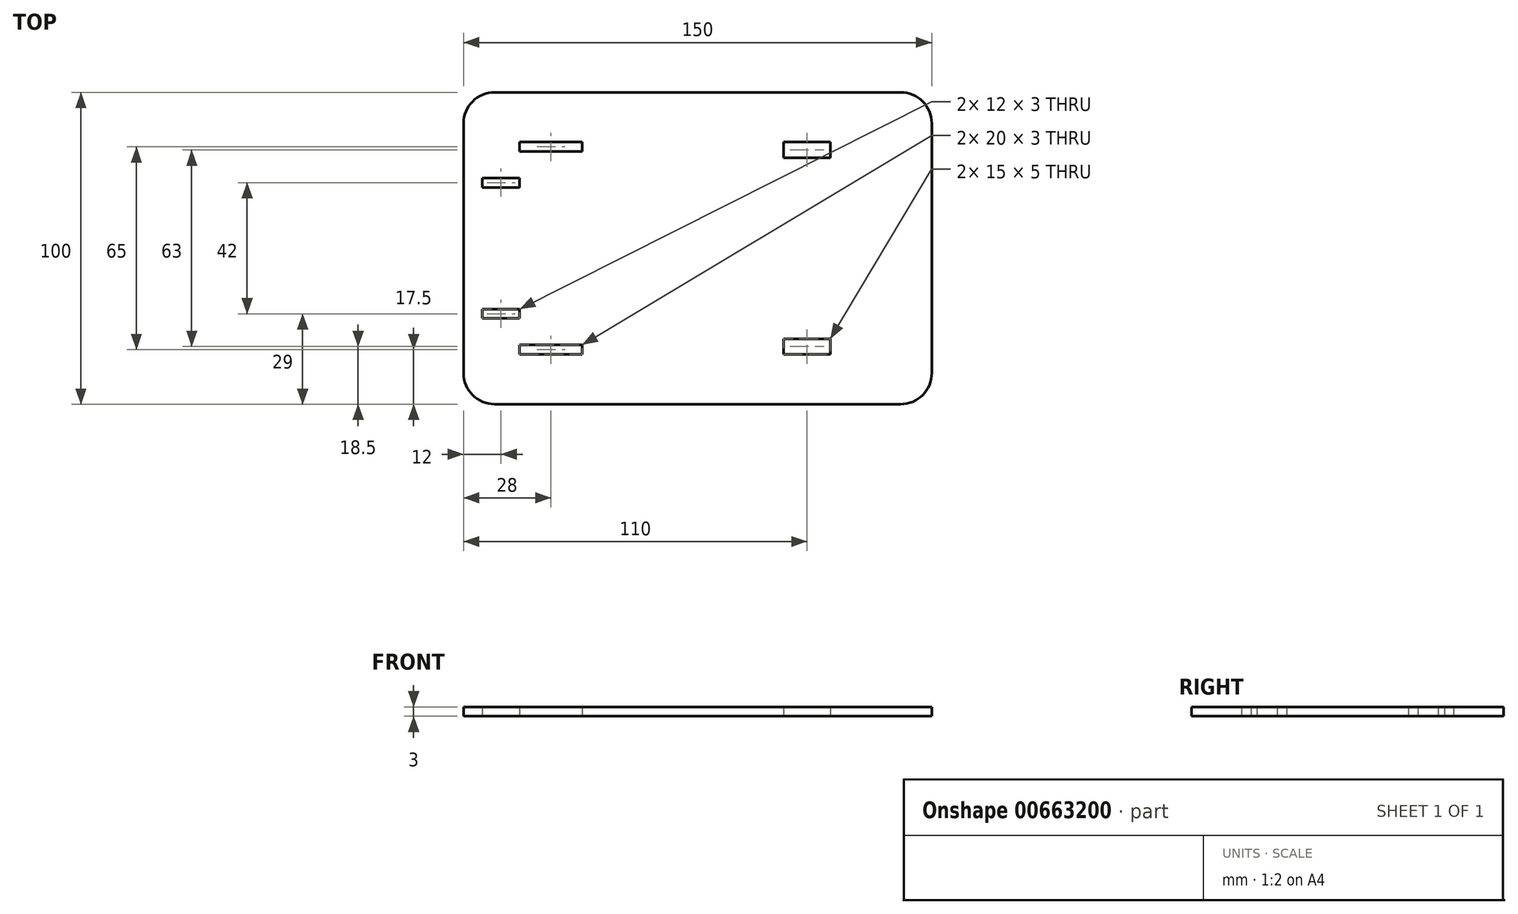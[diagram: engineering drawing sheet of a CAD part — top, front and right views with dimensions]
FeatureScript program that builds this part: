
annotation { "Feature Type Name" : "Feature", "Feature Type Description" : "" }
export const myFeature = defineFeature(function(context is Context, id is Id, definition is map)
    precondition{}
    {
        {
            var Q0;
            Q0=qCreatedBy(makeId("Top.planeOp"),FACE);
            var sketch = newSketch(context, id + "F0", { "sketchPlane" : qUnion([Q0])});
            skLineSegment(sketch, "E0.bottom", {"start": v(-65, 50) * mm, "end": v(65, 50) * mm});
            skLineSegment(sketch, "E0.top", {"start": v(-65, -50) * mm, "end": v(65, -50) * mm});
            skLineSegment(sketch, "E0.left", {"start": v(-75, 40) * mm, "end": v(-75, -40) * mm});
            skLineSegment(sketch, "E0.right", {"start": v(75, 40) * mm, "end": v(75, -40) * mm});
            skPoint(sketch, "E0.middle", {"position": v(0, 0) * mm});
            skLineSegment(sketch, "E1.bottom", {"start": v(-69, -19.5) * mm, "end": v(-57, -19.5) * mm});
            skLineSegment(sketch, "E1.top", {"start": v(-69, -22.5) * mm, "end": v(-57, -22.5) * mm});
            skLineSegment(sketch, "E1.left", {"start": v(-69, -19.5) * mm, "end": v(-69, -22.5) * mm});
            skLineSegment(sketch, "E1.right", {"start": v(-57, -19.5) * mm, "end": v(-57, -22.5) * mm});
            skLineSegment(sketch, "E2.bottom", {"start": v(-57, -31) * mm, "end": v(-37, -31) * mm});
            skLineSegment(sketch, "E2.top", {"start": v(-57, -34) * mm, "end": v(-37, -34) * mm});
            skLineSegment(sketch, "E2.left", {"start": v(-57, -31) * mm, "end": v(-57, -34) * mm});
            skLineSegment(sketch, "E2.right", {"start": v(-37, -31) * mm, "end": v(-37, -34) * mm});
            skLineSegment(sketch, "E3.bottom", {"start": v(27.5, -29) * mm, "end": v(42.5, -29) * mm});
            skLineSegment(sketch, "E3.top", {"start": v(27.5, -34) * mm, "end": v(42.5, -34) * mm});
            skLineSegment(sketch, "E3.left", {"start": v(27.5, -29) * mm, "end": v(27.5, -34) * mm});
            skLineSegment(sketch, "E3.right", {"start": v(42.5, -29) * mm, "end": v(42.5, -34) * mm});
            skLineSegment(sketch, "E4.MirrorCS", {"start": v(-37, 31) * mm, "end": v(-37, 34) * mm});
            skLineSegment(sketch, "E5.MirrorCS", {"start": v(-57, 31) * mm, "end": v(-57, 34) * mm});
            skLineSegment(sketch, "E6.MirrorCS", {"start": v(-69, 19.5) * mm, "end": v(-69, 22.5) * mm});
            skLineSegment(sketch, "E7.MirrorCS", {"start": v(-57, 19.5) * mm, "end": v(-57, 22.5) * mm});
            skLineSegment(sketch, "E8.MirrorCS", {"start": v(42.5, 29) * mm, "end": v(42.5, 34) * mm});
            skLineSegment(sketch, "E9.MirrorCS", {"start": v(27.5, 29) * mm, "end": v(27.5, 34) * mm});
            skLineSegment(sketch, "E10.MirrorCS", {"start": v(27.5, 29) * mm, "end": v(42.5, 29) * mm});
            skLineSegment(sketch, "E11.MirrorCS", {"start": v(-57, 34) * mm, "end": v(-37, 34) * mm});
            skLineSegment(sketch, "E12.MirrorCS", {"start": v(-69, 22.5) * mm, "end": v(-57, 22.5) * mm});
            skLineSegment(sketch, "E13.MirrorCS", {"start": v(-57, 31) * mm, "end": v(-37, 31) * mm});
            skLineSegment(sketch, "E14.MirrorCS", {"start": v(-69, 19.5) * mm, "end": v(-57, 19.5) * mm});
            skLineSegment(sketch, "E15.MirrorCS", {"start": v(27.5, 34) * mm, "end": v(42.5, 34) * mm});
            skPoint(sketch, "E16.visualSharp", {"position": v(-75, 50) * mm});
            skArc(sketch, "E16.filletArc", {"start": v(-65, 50) * mm, "mid": v(-72.07, 47.07) * mm, "end": v(-75, 40) * mm});
            skPoint(sketch, "E17.visualSharp", {"position": v(75, 50) * mm});
            skArc(sketch, "E17.filletArc", {"start": v(75, 40) * mm, "mid": v(72.07, 47.07) * mm, "end": v(65, 50) * mm});
            skPoint(sketch, "E18.visualSharp", {"position": v(75, -50) * mm});
            skArc(sketch, "E18.filletArc", {"start": v(65, -50) * mm, "mid": v(72.07, -47.07) * mm, "end": v(75, -40) * mm});
            skPoint(sketch, "E19.visualSharp", {"position": v(-75, -50) * mm});
            skArc(sketch, "E19.filletArc", {"start": v(-75, -40) * mm, "mid": v(-72.07, -47.07) * mm, "end": v(-65, -50) * mm});
            skSolve(sketch);
        }
        {
            var Q0;
            Q0 = qSketchRegion(id + "F0", true);
            extrude(context, id + "F1", {"entities" : qUnion([Q0]), "depth" : 3 * mm, "offsetDistance" : 25 * mm});
        }
    });
